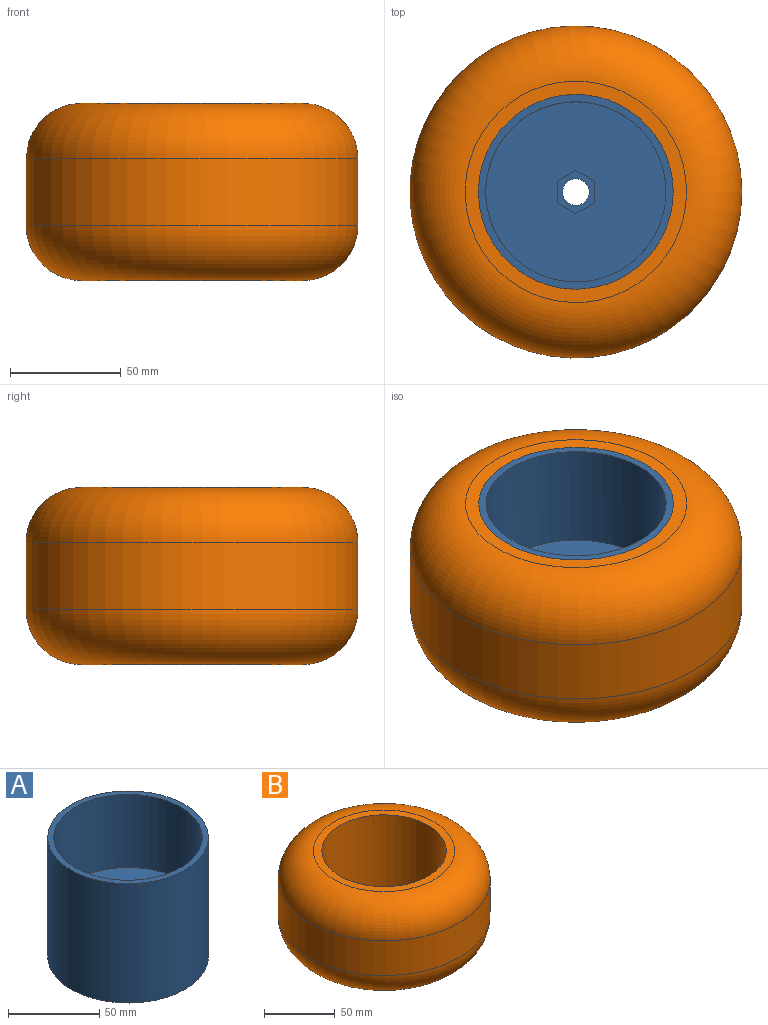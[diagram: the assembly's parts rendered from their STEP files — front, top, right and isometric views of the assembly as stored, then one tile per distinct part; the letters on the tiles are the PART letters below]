
ASSEMBLY  parts=2 mates=1
PART A: 15 faces, bbox 88x88x80 mm
  f0: cylinder r=40.71mm len=81.43mm, axis (0,0,-1), area 5116.1mm2, adj f4,f5
  f1: cylinder r=40.71mm len=81.43mm, axis (0,0,-1), area 12534.5mm2, adj f3,f12
  f2: cylinder r=44mm len=88mm, axis (0,0,-1), area 22116.8mm2, adj f3,f4
  f3: plane 88x88mm, normal (0,0,1), area 874.8mm2, adj f1,f2
  f4: plane 88x88mm, normal (0,0,-1), area 874.8mm2, adj f0,f2
  f5: plane 81.43x81.43mm, normal (0,0,-1), area 5093.8mm2, adj f0,f14
  f6: plane 8.5x6mm, normal (-0.5,-0.87,0), area 58.9mm2, adj f7,f11,f12,f13
  f7: plane 9.82x6mm, normal (-1,0,0), area 58.9mm2, adj f6,f8,f12,f13
  f8: plane 8.5x6mm, normal (-0.5,0.87,0), area 58.9mm2, adj f7,f9,f12,f13
  f9: plane 8.5x6mm, normal (0.5,0.87,0), area 58.9mm2, adj f8,f10,f12,f13
  f10: plane 9.82x6mm, normal (1,0,0), area 58.9mm2, adj f9,f11,f12,f13
  f11: plane 8.5x6mm, normal (0.5,-0.87,0), area 58.9mm2, adj f6,f10,f12,f13
  f12: plane 81.43x81.43mm, normal (0,0,1), area 4956.7mm2, adj f1,f6,f7,f8,f9,f10,f11
  f13: plane 19.63x17mm, normal (0,0,1), area 137.2mm2, adj f6,f7,f8,f9,f10,f11,f14
  f14: cylinder r=6mm len=12mm, axis (0,0,1), area 188.5mm2, adj f5,f13
PART B: 6 faces, bbox 162.4x162.4x80 mm
  f0: cylinder r=75mm len=150mm, axis (0,0,-1), area 14137.2mm2, adj f3,f4
  f1: plane 100x100mm, normal (0,0,1), area 1771.9mm2, adj f4,f5
  f2: plane 100x100mm, normal (0,0,-1), area 1771.9mm2, adj f3,f5
  f3: torus R=50mm, axis (0,0,1), area 16264mm2, adj f0,f2
  f4: torus R=50mm, axis (0,0,1), area 16264mm2, adj f0,f1
  f5: cylinder r=44mm len=88mm, axis (0,0,1), area 22116.8mm2, adj f1,f2
PLACE A t=(-51.74,-5.09,-2.82)mm
PLACE B t=(-51.74,-5.09,-2.82)mm
MATE fastened A.f2 <-> B.f0  axis (0,0,-1) through (-51.74,-5.09,-2.82)mm
